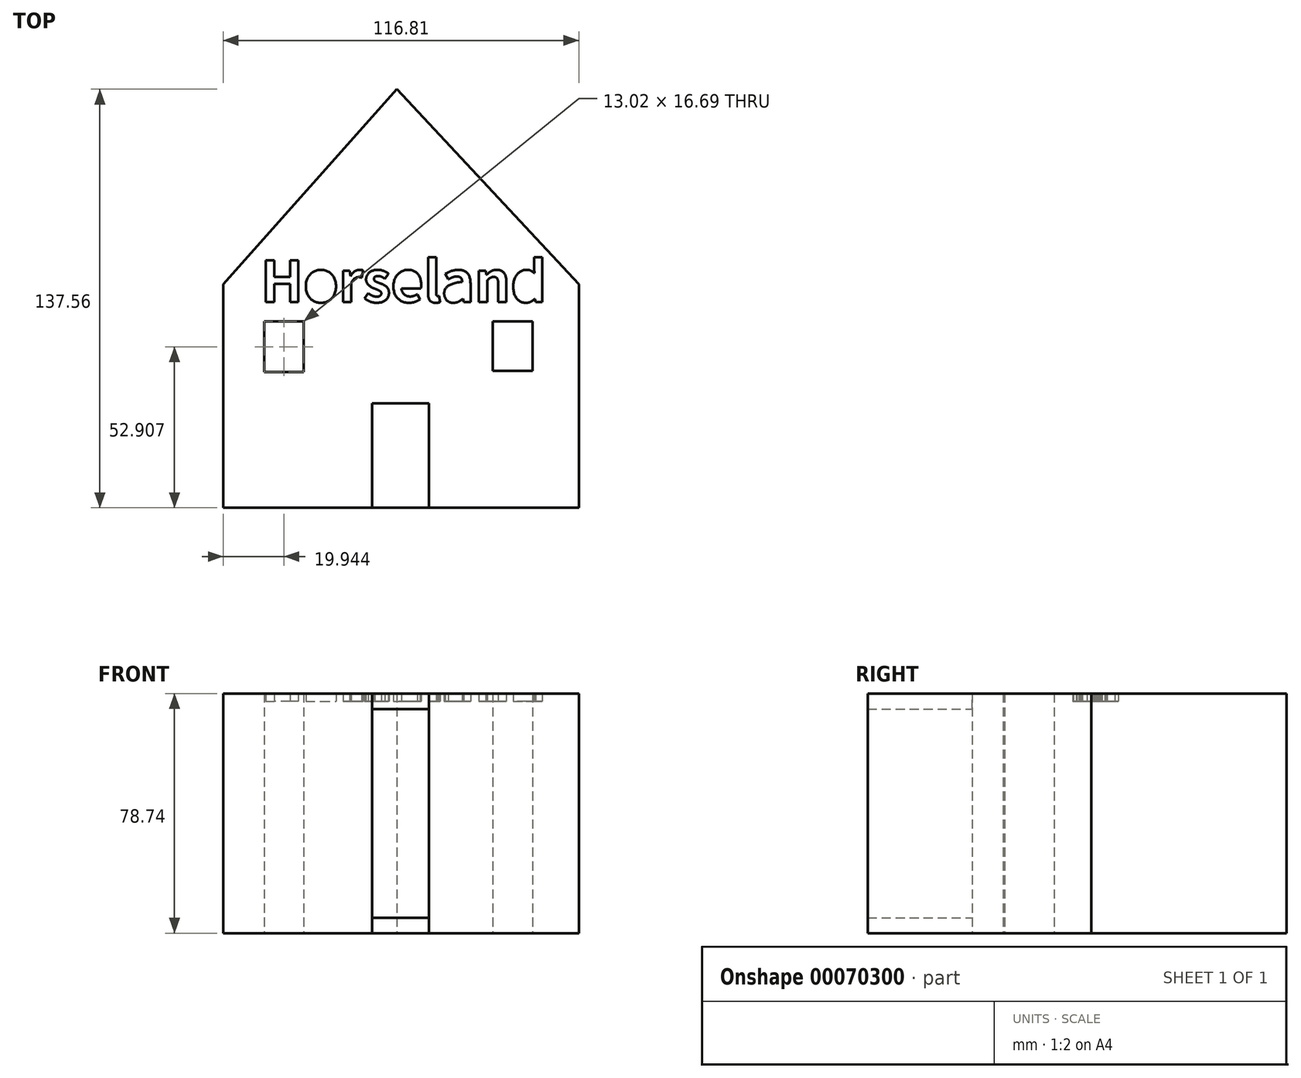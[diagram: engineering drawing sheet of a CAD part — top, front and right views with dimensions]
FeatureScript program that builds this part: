
annotation { "Feature Type Name" : "Feature", "Feature Type Description" : "" }
export const myFeature = defineFeature(function(context is Context, id is Id, definition is map)
    precondition{}
    {
        {
            var Q0;
            Q0=qCreatedBy(makeId("Top.planeOp"),FACE);
            var sketch = newSketch(context, id + "F0", { "sketchPlane" : qUnion([Q0])});
            skLineSegment(sketch, "E0.bottom", {"start": v(-56.98, 12.2) * mm, "end": v(59.83, 12.2) * mm});
            skLineSegment(sketch, "E0.top", {"start": v(-56.98, -61.25) * mm, "end": v(59.83, -61.25) * mm});
            skLineSegment(sketch, "E0.left", {"start": v(-56.98, 12.2) * mm, "end": v(-56.98, -61.25) * mm});
            skLineSegment(sketch, "E0.right", {"start": v(59.83, 12.2) * mm, "end": v(59.83, -61.25) * mm});
            skLineSegment(sketch, "E1", {"start": v(-56.98, 12.2) * mm, "end": v(0, 76.31) * mm});
            skLineSegment(sketch, "E2", {"start": v(0, 76.31) * mm, "end": v(59.83, 12.2) * mm});
            skLineSegment(sketch, "E3.bottom", {"start": v(31.54, 0) * mm, "end": v(44.57, 0) * mm});
            skLineSegment(sketch, "E3.top", {"start": v(31.54, -16.28) * mm, "end": v(44.57, -16.28) * mm});
            skLineSegment(sketch, "E3.left", {"start": v(31.54, 0) * mm, "end": v(31.54, -16.28) * mm});
            skLineSegment(sketch, "E3.right", {"start": v(44.57, 0) * mm, "end": v(44.57, -16.28) * mm});
            skLineSegment(sketch, "E4.bottom", {"start": v(-43.55, 0) * mm, "end": v(-30.52, 0) * mm});
            skLineSegment(sketch, "E4.top", {"start": v(-43.55, -16.69) * mm, "end": v(-30.52, -16.69) * mm});
            skLineSegment(sketch, "E4.left", {"start": v(-43.55, 0) * mm, "end": v(-43.55, -16.69) * mm});
            skLineSegment(sketch, "E4.right", {"start": v(-30.52, 0) * mm, "end": v(-30.52, -16.69) * mm});
            skLineSegment(sketch, "E5.bottom", {"start": v(-8.14, -61.25) * mm, "end": v(10.58, -61.25) * mm});
            skLineSegment(sketch, "E5.top", {"start": v(-8.14, -26.86) * mm, "end": v(10.58, -26.86) * mm});
            skLineSegment(sketch, "E5.left", {"start": v(-8.14, -61.25) * mm, "end": v(-8.14, -26.86) * mm});
            skLineSegment(sketch, "E5.right", {"start": v(10.58, -61.25) * mm, "end": v(10.58, -26.86) * mm});
            skCircle(sketch, "E6", {"center": v(7.08, -46.02) * mm, "radius": 1.62 * mm});
            skSolve(sketch);
        }
        {
            var Q0;
            Q0=makeQuery(id+"F0.imprint","IMPRINT",FACE,{"disambiguationData":[TD([[makeQuery(id+"F0.imprint","IMPRINT",EDGE,{"derivedFrom":sQuery(id+"F0.wireOp",EDGE,"E0.bottom")}),-1.0]])]});
            var Q1;
            Q1=makeQuery(id+"F0.imprint","IMPRINT",FACE,{"disambiguationData":[TD([[makeQuery(id+"F0.imprint","IMPRINT",EDGE,{"derivedFrom":sQuery(id+"F0.wireOp",EDGE,"E0.bottom")}),1.0]])]});
            extrude(context, id + "F1", {"entities" : qUnion([Q0, Q1]), "depth" : 76.2 * mm});
        }
        {
            var Q0;
            Q0=qCreatedBy(makeId("Top.planeOp"),FACE);
            var sketch = newSketch(context, id + "F2", { "sketchPlane" : qUnion([Q0])});
            skLineSegment(sketch, "E7.bottom", {"start": v(-7.56, -27.51) * mm, "end": v(10.07, -27.51) * mm});
            skLineSegment(sketch, "E7.top", {"start": v(-7.56, -60.38) * mm, "end": v(10.07, -60.38) * mm});
            skLineSegment(sketch, "E7.left", {"start": v(-7.56, -27.51) * mm, "end": v(-7.56, -60.38) * mm});
            skLineSegment(sketch, "E7.right", {"start": v(10.07, -27.51) * mm, "end": v(10.07, -60.38) * mm});
            skSolve(sketch);
        }
        {
            var Q0;
            Q0=makeQuery(id+"F1.opExtrude","CAP_FACE",FACE,{"disambiguationData":[OSD([sQuery(id+"F0.wireOp",EDGE,"E0.top"),sQuery(id+"F0.wireOp",EDGE,"E0.left"),sQuery(id+"F0.wireOp",EDGE,"E0.right"),sQuery(id+"F0.wireOp",EDGE,"E1"),sQuery(id+"F0.wireOp",EDGE,"E2"),sQuery(id+"F0.wireOp",EDGE,"E3.bottom"),sQuery(id+"F0.wireOp",EDGE,"E3.top"),sQuery(id+"F0.wireOp",EDGE,"E3.left"),sQuery(id+"F0.wireOp",EDGE,"E3.right"),sQuery(id+"F0.wireOp",EDGE,"E4.bottom"),sQuery(id+"F0.wireOp",EDGE,"E4.top"),sQuery(id+"F0.wireOp",EDGE,"E4.left"),sQuery(id+"F0.wireOp",EDGE,"E4.right"),sQuery(id+"F0.wireOp",EDGE,"E5.top"),sQuery(id+"F0.wireOp",EDGE,"E5.left"),sQuery(id+"F0.wireOp",EDGE,"E5.right")])],"isStart":false});
            var sketch = newSketch(context, id + "F3", { "sketchPlane" : qUnion([Q0])});
            skText(sketch, "E8", { "text": "Horseland", "fontName": "NotoSansCJKkr-Bold.otf"});
            const initialGuessF3  = {"E8": [-0.04466, 0.00635, 1, 0, 0.0133]};
            skSetInitialGuess(sketch, initialGuessF3);
            skSolve(sketch);
        }
        {
            var Q0;
            Q0=makeQuery(id+"F3.imprint","IMPRINT",FACE,{"disambiguationData":[TD([[makeQuery(id+"F3.imprint","IMPRINT",EDGE,{"derivedFrom":sQuery(id+"F3.wireOp",EDGE,"E8.sketch_text.stroke-0")}),-1.0]])]});
            extrude(context, id + "F4", {"entities" : qUnion([Q0]), "operationType" : NewBodyOperationType.ADD, "depth" : 2.54 * mm});
        }
        {
            var Q0;
            Q0=makeQuery(id+"F2.imprint","IMPRINT",FACE,{"disambiguationData":[TD([[makeQuery(id+"F2.imprint","IMPRINT",EDGE,{"derivedFrom":sQuery(id+"F2.wireOp",EDGE,"E7.bottom")}),-1.0]])]});
            extrude(context, id + "F5", {"entities" : qUnion([Q0]), "depth" : 25.4 * mm});
        }
        {
            var Q0;
            Q0=makeQuery(id+"F4.opExtrude","CAP_FACE",FACE,{"disambiguationData":[OSD([sQuery(id+"F0.wireOp",EDGE,"E0.top"),sQuery(id+"F0.wireOp",EDGE,"E0.left"),sQuery(id+"F0.wireOp",EDGE,"E0.right"),sQuery(id+"F0.wireOp",EDGE,"E1"),sQuery(id+"F0.wireOp",EDGE,"E2"),sQuery(id+"F0.wireOp",EDGE,"E3.bottom"),sQuery(id+"F0.wireOp",EDGE,"E3.top"),sQuery(id+"F0.wireOp",EDGE,"E3.left"),sQuery(id+"F0.wireOp",EDGE,"E3.right"),sQuery(id+"F0.wireOp",EDGE,"E4.bottom"),sQuery(id+"F0.wireOp",EDGE,"E4.top"),sQuery(id+"F0.wireOp",EDGE,"E4.left"),sQuery(id+"F0.wireOp",EDGE,"E4.right"),sQuery(id+"F0.wireOp",EDGE,"E5.top"),sQuery(id+"F0.wireOp",EDGE,"E5.left"),sQuery(id+"F0.wireOp",EDGE,"E5.right"),sQuery(id+"F3.wireOp",EDGE,"E8.sketch_text.stroke-0"),sQuery(id+"F3.wireOp",EDGE,"E8.sketch_text.stroke-1"),sQuery(id+"F3.wireOp",EDGE,"E8.sketch_text.stroke-2"),sQuery(id+"F3.wireOp",EDGE,"E8.sketch_text.stroke-3"),sQuery(id+"F3.wireOp",EDGE,"E8.sketch_text.stroke-4"),sQuery(id+"F3.wireOp",EDGE,"E8.sketch_text.stroke-5"),sQuery(id+"F3.wireOp",EDGE,"E8.sketch_text.stroke-6"),sQuery(id+"F3.wireOp",EDGE,"E8.sketch_text.stroke-7"),sQuery(id+"F3.wireOp",EDGE,"E8.sketch_text.stroke-8"),sQuery(id+"F3.wireOp",EDGE,"E8.sketch_text.stroke-9"),sQuery(id+"F3.wireOp",EDGE,"E8.sketch_text.stroke-10"),sQuery(id+"F3.wireOp",EDGE,"E8.sketch_text.stroke-11"),sQuery(id+"F3.wireOp",EDGE,"E8.sketch_text.stroke-12"),sQuery(id+"F3.wireOp",EDGE,"E8.sketch_text.stroke-13"),sQuery(id+"F3.wireOp",EDGE,"E8.sketch_text.stroke-14"),sQuery(id+"F3.wireOp",EDGE,"E8.sketch_text.stroke-15"),sQuery(id+"F3.wireOp",EDGE,"E8.sketch_text.stroke-20"),sQuery(id+"F3.wireOp",EDGE,"E8.sketch_text.stroke-21"),sQuery(id+"F3.wireOp",EDGE,"E8.sketch_text.stroke-22"),sQuery(id+"F3.wireOp",EDGE,"E8.sketch_text.stroke-23"),sQuery(id+"F3.wireOp",EDGE,"E8.sketch_text.stroke-24"),sQuery(id+"F3.wireOp",EDGE,"E8.sketch_text.stroke-25"),sQuery(id+"F3.wireOp",EDGE,"E8.sketch_text.stroke-26"),sQuery(id+"F3.wireOp",EDGE,"E8.sketch_text.stroke-27"),sQuery(id+"F3.wireOp",EDGE,"E8.sketch_text.stroke-28"),sQuery(id+"F3.wireOp",EDGE,"E8.sketch_text.stroke-29"),sQuery(id+"F3.wireOp",EDGE,"E8.sketch_text.stroke-30"),sQuery(id+"F3.wireOp",EDGE,"E8.sketch_text.stroke-31"),sQuery(id+"F3.wireOp",EDGE,"E8.sketch_text.stroke-32"),sQuery(id+"F3.wireOp",EDGE,"E8.sketch_text.stroke-33"),sQuery(id+"F3.wireOp",EDGE,"E8.sketch_text.stroke-34"),sQuery(id+"F3.wireOp",EDGE,"E8.sketch_text.stroke-35"),sQuery(id+"F3.wireOp",EDGE,"E8.sketch_text.stroke-36"),sQuery(id+"F3.wireOp",EDGE,"E8.sketch_text.stroke-37"),sQuery(id+"F3.wireOp",EDGE,"E8.sketch_text.stroke-38"),sQuery(id+"F3.wireOp",EDGE,"E8.sketch_text.stroke-39"),sQuery(id+"F3.wireOp",EDGE,"E8.sketch_text.stroke-40"),sQuery(id+"F3.wireOp",EDGE,"E8.sketch_text.stroke-41"),sQuery(id+"F3.wireOp",EDGE,"E8.sketch_text.stroke-42"),sQuery(id+"F3.wireOp",EDGE,"E8.sketch_text.stroke-43"),sQuery(id+"F3.wireOp",EDGE,"E8.sketch_text.stroke-44"),sQuery(id+"F3.wireOp",EDGE,"E8.sketch_text.stroke-45"),sQuery(id+"F3.wireOp",EDGE,"E8.sketch_text.stroke-46"),sQuery(id+"F3.wireOp",EDGE,"E8.sketch_text.stroke-47"),sQuery(id+"F3.wireOp",EDGE,"E8.sketch_text.stroke-48"),sQuery(id+"F3.wireOp",EDGE,"E8.sketch_text.stroke-49"),sQuery(id+"F3.wireOp",EDGE,"E8.sketch_text.stroke-50"),sQuery(id+"F3.wireOp",EDGE,"E8.sketch_text.stroke-51"),sQuery(id+"F3.wireOp",EDGE,"E8.sketch_text.stroke-52"),sQuery(id+"F3.wireOp",EDGE,"E8.sketch_text.stroke-53"),sQuery(id+"F3.wireOp",EDGE,"E8.sketch_text.stroke-57"),sQuery(id+"F3.wireOp",EDGE,"E8.sketch_text.stroke-58"),sQuery(id+"F3.wireOp",EDGE,"E8.sketch_text.stroke-59"),sQuery(id+"F3.wireOp",EDGE,"E8.sketch_text.stroke-60"),sQuery(id+"F3.wireOp",EDGE,"E8.sketch_text.stroke-61"),sQuery(id+"F3.wireOp",EDGE,"E8.sketch_text.stroke-62"),sQuery(id+"F3.wireOp",EDGE,"E8.sketch_text.stroke-63"),sQuery(id+"F3.wireOp",EDGE,"E8.sketch_text.stroke-64"),sQuery(id+"F3.wireOp",EDGE,"E8.sketch_text.stroke-65"),sQuery(id+"F3.wireOp",EDGE,"E8.sketch_text.stroke-66"),sQuery(id+"F3.wireOp",EDGE,"E8.sketch_text.stroke-67"),sQuery(id+"F3.wireOp",EDGE,"E8.sketch_text.stroke-68"),sQuery(id+"F3.wireOp",EDGE,"E8.sketch_text.stroke-69"),sQuery(id+"F3.wireOp",EDGE,"E8.sketch_text.stroke-70"),sQuery(id+"F3.wireOp",EDGE,"E8.sketch_text.stroke-71"),sQuery(id+"F3.wireOp",EDGE,"E8.sketch_text.stroke-72"),sQuery(id+"F3.wireOp",EDGE,"E8.sketch_text.stroke-73"),sQuery(id+"F3.wireOp",EDGE,"E8.sketch_text.stroke-74"),sQuery(id+"F3.wireOp",EDGE,"E8.sketch_text.stroke-75"),sQuery(id+"F3.wireOp",EDGE,"E8.sketch_text.stroke-76"),sQuery(id+"F3.wireOp",EDGE,"E8.sketch_text.stroke-81"),sQuery(id+"F3.wireOp",EDGE,"E8.sketch_text.stroke-82"),sQuery(id+"F3.wireOp",EDGE,"E8.sketch_text.stroke-83"),sQuery(id+"F3.wireOp",EDGE,"E8.sketch_text.stroke-84"),sQuery(id+"F3.wireOp",EDGE,"E8.sketch_text.stroke-85"),sQuery(id+"F3.wireOp",EDGE,"E8.sketch_text.stroke-86"),sQuery(id+"F3.wireOp",EDGE,"E8.sketch_text.stroke-87"),sQuery(id+"F3.wireOp",EDGE,"E8.sketch_text.stroke-88"),sQuery(id+"F3.wireOp",EDGE,"E8.sketch_text.stroke-89"),sQuery(id+"F3.wireOp",EDGE,"E8.sketch_text.stroke-90"),sQuery(id+"F3.wireOp",EDGE,"E8.sketch_text.stroke-91"),sQuery(id+"F3.wireOp",EDGE,"E8.sketch_text.stroke-92"),sQuery(id+"F3.wireOp",EDGE,"E8.sketch_text.stroke-93"),sQuery(id+"F3.wireOp",EDGE,"E8.sketch_text.stroke-94"),sQuery(id+"F3.wireOp",EDGE,"E8.sketch_text.stroke-95"),sQuery(id+"F3.wireOp",EDGE,"E8.sketch_text.stroke-96"),sQuery(id+"F3.wireOp",EDGE,"E8.sketch_text.stroke-97"),sQuery(id+"F3.wireOp",EDGE,"E8.sketch_text.stroke-98"),sQuery(id+"F3.wireOp",EDGE,"E8.sketch_text.stroke-99"),sQuery(id+"F3.wireOp",EDGE,"E8.sketch_text.stroke-100"),sQuery(id+"F3.wireOp",EDGE,"E8.sketch_text.stroke-101"),sQuery(id+"F3.wireOp",EDGE,"E8.sketch_text.stroke-102"),sQuery(id+"F3.wireOp",EDGE,"E8.sketch_text.stroke-103"),sQuery(id+"F3.wireOp",EDGE,"E8.sketch_text.stroke-104")])],"isStart":false});
            var sketch = newSketch(context, id + "F6", { "sketchPlane" : qUnion([Q0])});
            skLineSegment(sketch, "E9.bottom", {"start": v(-8.14, -26.86) * mm, "end": v(10.58, -26.86) * mm});
            skLineSegment(sketch, "E9.top", {"start": v(-8.14, -61.25) * mm, "end": v(10.58, -61.25) * mm});
            skLineSegment(sketch, "E9.left", {"start": v(-8.14, -26.86) * mm, "end": v(-8.14, -61.25) * mm});
            skLineSegment(sketch, "E9.right", {"start": v(10.58, -26.86) * mm, "end": v(10.58, -61.25) * mm});
            skSolve(sketch);
        }
        {
            var Q0;
            Q0=makeQuery(id+"F6.imprint","IMPRINT",FACE,{"disambiguationData":[TD([[makeQuery(id+"F6.imprint","IMPRINT",EDGE,{"derivedFrom":sQuery(id+"F6.wireOp",EDGE,"E9.bottom")}),-1.0]])]});
            extrude(context, id + "F7", {"entities" : qUnion([Q0]), "oppositeDirection" : true, "depth" : 5.08 * mm});
        }
        {
            var Q0;
            Q0=makeQuery(id+"F5.opExtrude","SWEPT_BODY",BODY,{"disambiguationData":[OSD([sQuery(id+"F2.wireOp",EDGE,"E7.bottom"),sQuery(id+"F2.wireOp",EDGE,"E7.top"),sQuery(id+"F2.wireOp",EDGE,"E7.left"),sQuery(id+"F2.wireOp",EDGE,"E7.right")])]});
            deleteBodies(context, id + "F8", {"entities" : qUnion([Q0])});
        }
        {
            var Q0;
            Q0=makeQuery(id+"F1.opExtrude","CAP_FACE",FACE,{"disambiguationData":[OSD([sQuery(id+"F0.wireOp",EDGE,"E0.top"),sQuery(id+"F0.wireOp",EDGE,"E0.left"),sQuery(id+"F0.wireOp",EDGE,"E0.right"),sQuery(id+"F0.wireOp",EDGE,"E1"),sQuery(id+"F0.wireOp",EDGE,"E2"),sQuery(id+"F0.wireOp",EDGE,"E3.bottom"),sQuery(id+"F0.wireOp",EDGE,"E3.top"),sQuery(id+"F0.wireOp",EDGE,"E3.left"),sQuery(id+"F0.wireOp",EDGE,"E3.right"),sQuery(id+"F0.wireOp",EDGE,"E4.bottom"),sQuery(id+"F0.wireOp",EDGE,"E4.top"),sQuery(id+"F0.wireOp",EDGE,"E4.left"),sQuery(id+"F0.wireOp",EDGE,"E4.right"),sQuery(id+"F0.wireOp",EDGE,"E5.top"),sQuery(id+"F0.wireOp",EDGE,"E5.left"),sQuery(id+"F0.wireOp",EDGE,"E5.right")])],"isStart":true});
            var sketch = newSketch(context, id + "F9", { "sketchPlane" : qUnion([Q0])});
            skLineSegment(sketch, "E10.bottom", {"start": v(10.58, 26.86) * mm, "end": v(-8.14, 26.86) * mm});
            skLineSegment(sketch, "E10.top", {"start": v(10.58, 61.25) * mm, "end": v(-8.14, 61.25) * mm});
            skLineSegment(sketch, "E10.left", {"start": v(10.58, 26.86) * mm, "end": v(10.58, 61.25) * mm});
            skLineSegment(sketch, "E10.right", {"start": v(-8.14, 26.86) * mm, "end": v(-8.14, 61.25) * mm});
            skSolve(sketch);
        }
        {
            var Q0;
            Q0=makeQuery(id+"F9.imprint","IMPRINT",FACE,{"disambiguationData":[TD([[makeQuery(id+"F9.imprint","IMPRINT",EDGE,{"derivedFrom":sQuery(id+"F9.wireOp",EDGE,"E10.bottom")}),1.0]])]});
            extrude(context, id + "F10", {"entities" : qUnion([Q0]), "oppositeDirection" : true, "depth" : 5.08 * mm});
        }
    });
